# Revit family: Sink-Drop_In-Lavatory-KOHLER-Rhythm_Oval-K-2603
name_source: partatom
category: Plumbing Fixtures
revit_build: Autodesk Revit 2017 (Build: 20160225_1515(x64)
units: mm (PartAtom-declared; Revit-internal decimal feet)

## family parameters
Cut with Voids When Loaded = No
Host = Face
OmniClass Number = 23.31.13.00
OmniClass Title = Sinks
Part Type = Normal
Room Calculation Point = No
Round Connector Dimension = Use Diameter
Shared = No

## types (2) — shared parameters
ADA Compliant = Yes
Assembly Code = D2010400
CW Connection = No
Cold Water Inlet = Cold Water Inlet
Date Modified = 11/27/2020
Default Elevation = 36"
Drain Included = No
Finish = Kohler-Metal-NA-Stainless
HW Connection = No
Height = 5 15/16"
Hot Water Inlet = Hot Water Inlet
Length = 15 1/4"
Manufacturer = KOHLER Co.
Master Format 2014 = 22 41 16
Master Format 2014 Name = Residential Lavatories and Sinks
Material = Stainless Steel Construction
Product Documentation Link = https://www.us.kohler.com
Product Name = Rhythm Oval
Product Page URL = http://www.us.kohler.com
URL = https://www.us.kohler.com
Vent Connection = No
Waste Connection = Yes
Waste Water Outlet = Waste Water Outlet
WaterSense Certified = No
Width = 23 1/8"

## per-type parameters (varying)
| type | Description | Model | Type |
| Satin Finish, NA-Stainless Steel | Drop-in bathroom sink with satin finish | K-2603-SU-NA | 1 |
| Mirror Finish, NA-Stainless Steel | Drop-in bathroom sink with mirror finish | K-2603-MU-NA | 2 |

## geometry (parser evidence)
native form markers: Sweep x4
no freeform markers — native parametric forms only
